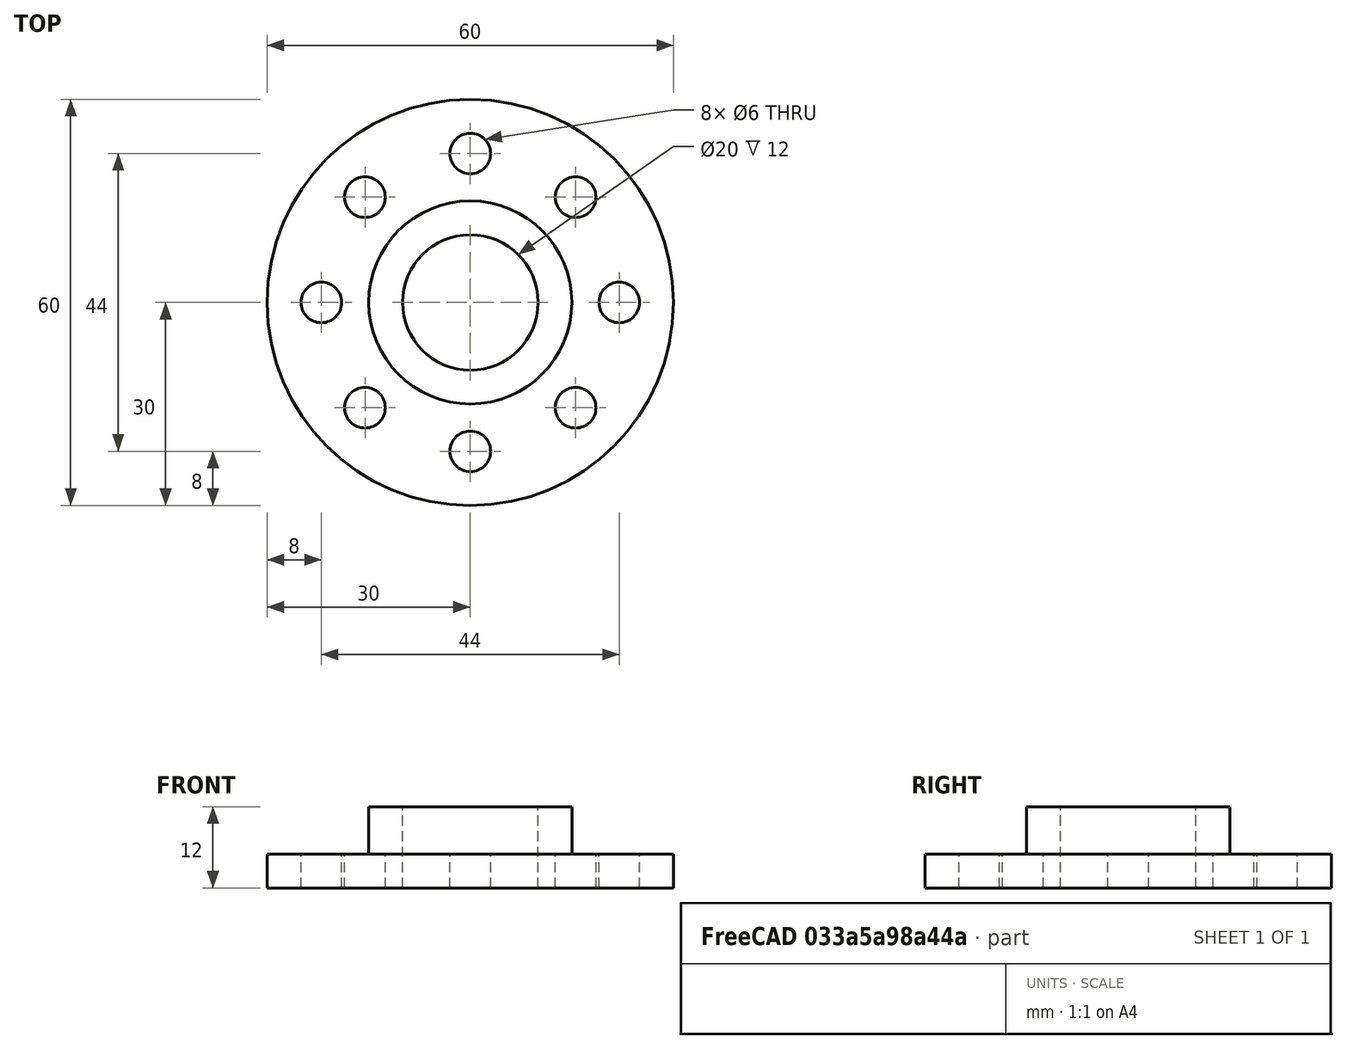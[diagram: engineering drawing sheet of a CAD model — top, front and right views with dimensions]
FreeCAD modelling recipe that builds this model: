
FCSTD DOCUMENT  (FreeCAD 0.18R16146 (Git))
Label: brida_dani
License: All rights reserved
LicenseURL: http://en.wikipedia.org/wiki/All_rights_reserved
objects: Part::Cylinder×4, Part::Cut×2, Part::MultiFuse×1, Part::FeaturePython×1
note: 8 computed .brp shape members not serialized (recipe doc carries the construction recipe); baked Part::Feature solids carry a one-line shape summary decoded from their .brp

FEATURE [Part::Cylinder] Cylinder  label="brida"
  Angle = 360
  AttacherType = Attacher::AttachEngine3D
  Height = 5
  Radius = 30
FEATURE [Part::Cylinder] Cylinder001  label=" tuberia exterior"
  Angle = 360
  AttacherType = Attacher::AttachEngine3D
  Height = 12
  Radius = 15
FEATURE [Part::MultiFuse] Fusion
  Refine = true
  Shapes = -> [Cylinder,Cylinder001]
FEATURE [Part::Cylinder] Cylinder002  label="tubo interior"
  Angle = 360
  AttacherType = Attacher::AttachEngine3D
  Height = 30
  Placement = pos=(0,0,-1) rot=(0,0,1;0rad)
  Radius = 10
FEATURE [Part::Cut] Cut  label="brida sin taladro"
  Base = -> Fusion
  Refine = true
  Tool = -> Cylinder002
FEATURE [Part::Cylinder] Cylinder003  label="taladro master"
  Angle = 360
  AttacherType = Attacher::AttachEngine3D
  Height = 10
  Placement = pos=(22,0,-1) rot=(0,0,1;0rad)
  Radius = 3
FEATURE [Part::FeaturePython] Array  # Draft array (typed FeaturePython)
  Angle = 360
  ArrayType = 1
  Axis = (0,0,1)
  Base = -> Cylinder003
  Center = (0,0,0)
  Fuse = false
  IntervalAxis = (0,0,0)
  IntervalX = (1,0,0)
  IntervalY = (0,1,0)
  IntervalZ = (0,0,1)
  NumberPolar = 8
  NumberX = 2
  NumberY = 2
  NumberZ = 1
FEATURE [Part::Cut] Cut001  label="brida entera"
  Base = -> Cut
  Refine = true
  Tool = -> Array
